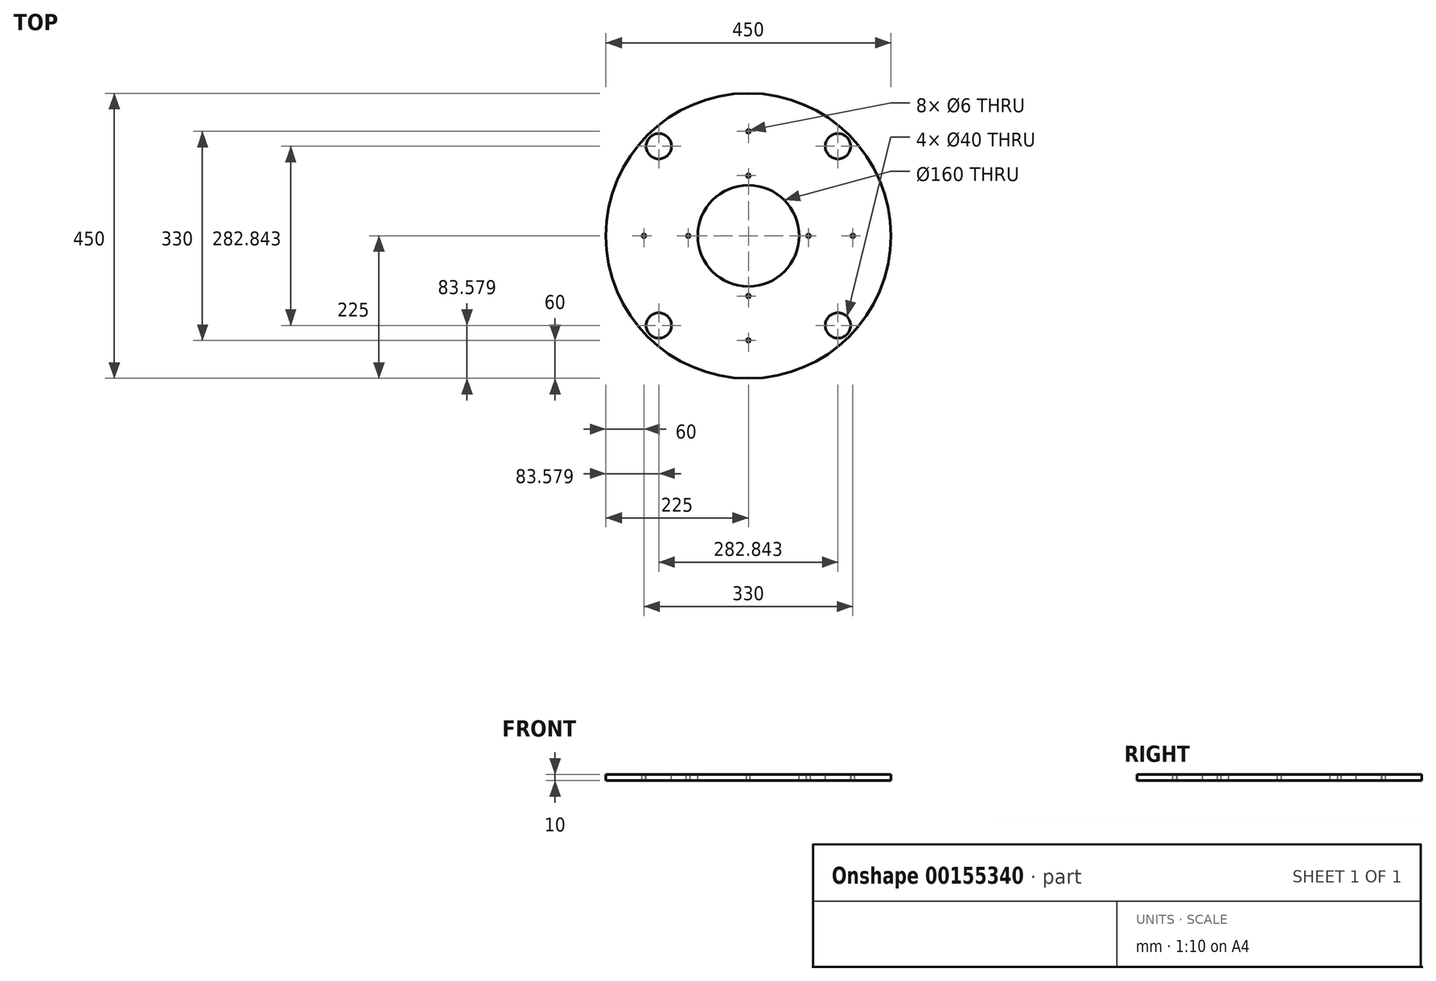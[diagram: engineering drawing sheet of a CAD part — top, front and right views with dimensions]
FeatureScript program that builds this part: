
annotation { "Feature Type Name" : "Feature", "Feature Type Description" : "" }
export const myFeature = defineFeature(function(context is Context, id is Id, definition is map)
    precondition{}
    {
        {
            var Q0;
            Q0=qCreatedBy(makeId("Top.planeOp"),FACE);
            var sketch = newSketch(context, id + "F0", { "sketchPlane" : qUnion([Q0])});
            skCircle(sketch, "E0", {"center": v(0, 0) * mm, "radius": 225 * mm});
            skSolve(sketch);
        }
        {
            var Q0;
            Q0 = qSketchRegion(id + "F0", true);
            extrude(context, id + "F1", {"entities" : qUnion([Q0]), "depth" : 10 * mm});
        }
        {
            var Q0;
            Q0=makeQuery(id+"F1.opExtrude","CAP_FACE",FACE,{"disambiguationData":[OSD([sQuery(id+"F0.wireOp",EDGE,"E0")])],"isStart":false});
            var sketch = newSketch(context, id + "F2", { "sketchPlane" : qUnion([Q0])});
            skCircle(sketch, "E1", {"center": v(0, 0) * mm, "radius": 80 * mm});
            skLineSegment(sketch, "E2", {"start": v(0, 0) * mm, "end": v(-253.44, 0) * mm, "construction": true});
            skLineSegment(sketch, "E3", {"start": v(0, 0) * mm, "end": v(0, -244.5) * mm, "construction": true});
            skCircle(sketch, "E4", {"center": v(-95, 0) * mm, "radius": 3 * mm});
            skCircle(sketch, "E5", {"center": v(-165, 0) * mm, "radius": 3 * mm});
            skLineSegment(sketch, "E6", {"start": v(0, 0) * mm, "end": v(-188.84, -188.84) * mm, "construction": true});
            skCircle(sketch, "E7.MirrorC", {"center": v(0, -95) * mm, "radius": 3 * mm});
            skCircle(sketch, "E8.MirrorC", {"center": v(0, -165) * mm, "radius": 3 * mm});
            skLineSegment(sketch, "E9", {"start": v(0, 0) * mm, "end": v(-243.64, 243.64) * mm, "construction": true});
            skCircle(sketch, "E10.MirrorC", {"center": v(0, 165) * mm, "radius": 3 * mm});
            skCircle(sketch, "E11.MirrorC", {"center": v(0, 95) * mm, "radius": 3 * mm});
            skCircle(sketch, "E12.MirrorC", {"center": v(95, 0) * mm, "radius": 3 * mm});
            skCircle(sketch, "E13.MirrorC", {"center": v(165, 0) * mm, "radius": 3 * mm});
            skCircle(sketch, "E14", {"center": v(-141.42, -141.42) * mm, "radius": 20 * mm});
            skCircle(sketch, "E15.MirrorC", {"center": v(-141.42, 141.42) * mm, "radius": 20 * mm});
            skCircle(sketch, "E16.MirrorC", {"center": v(141.42, -141.42) * mm, "radius": 20 * mm});
            skCircle(sketch, "E17.MirrorC", {"center": v(141.42, 141.42) * mm, "radius": 20 * mm});
            skSolve(sketch);
        }
        {
            var Q0;
            Q0 = qSketchRegion(id + "F2", true);
            extrude(context, id + "F3", {"entities" : qUnion([Q0]), "operationType" : NewBodyOperationType.REMOVE, "endBound" : BoundingType.THROUGH_ALL, "oppositeDirection" : true, "depth" : 25 * mm});
        }
    });
